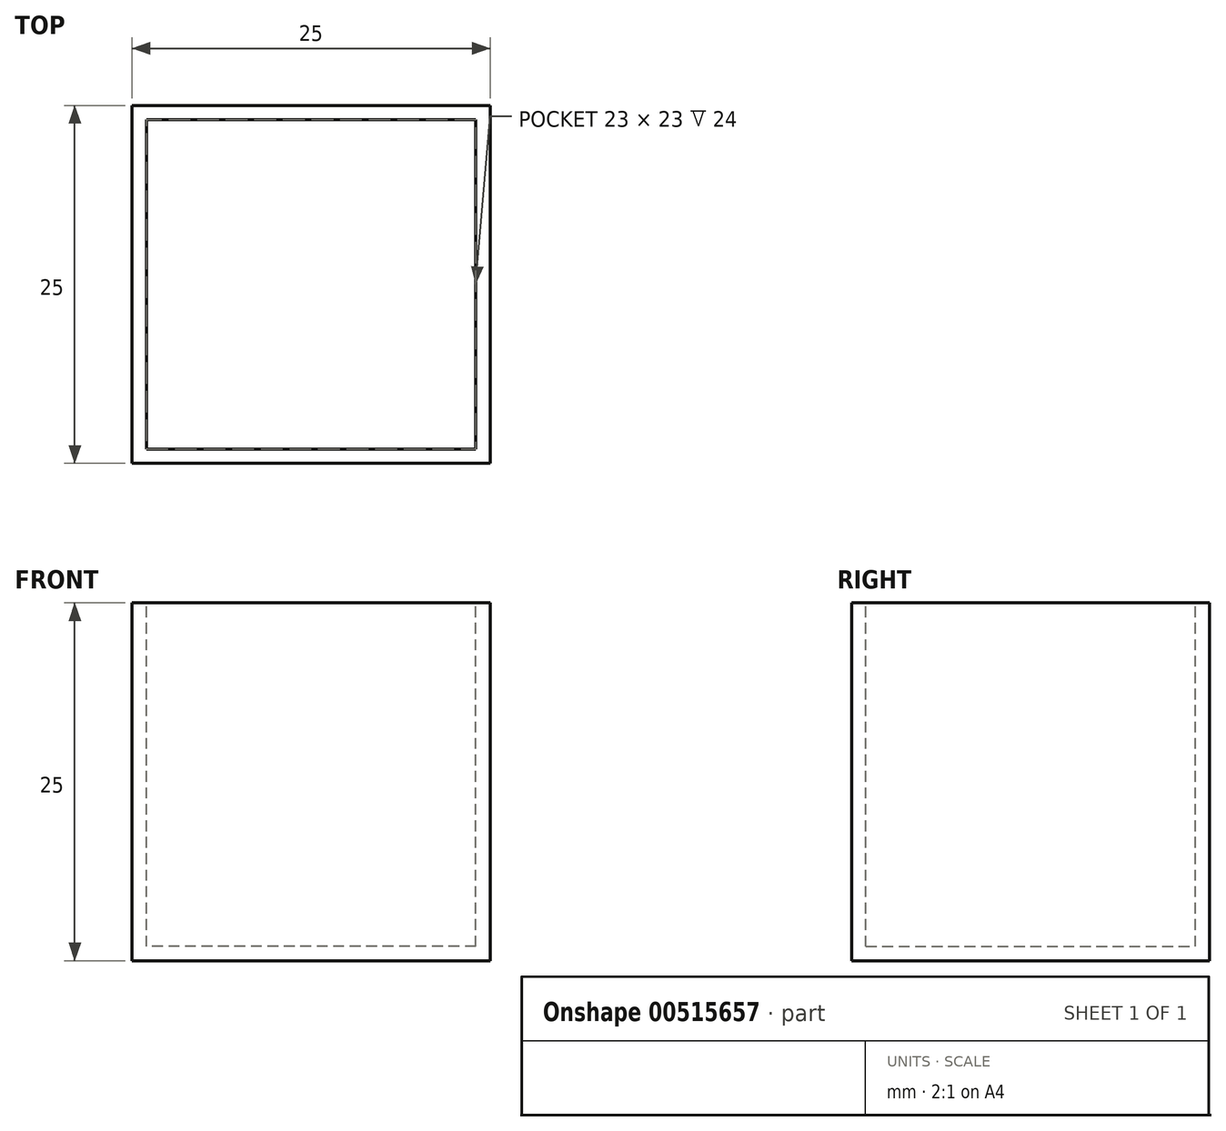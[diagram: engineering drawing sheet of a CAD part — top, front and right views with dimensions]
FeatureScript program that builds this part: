
annotation { "Feature Type Name" : "Feature", "Feature Type Description" : "" }
export const myFeature = defineFeature(function(context is Context, id is Id, definition is map)
    precondition{}
    {
        {
            var Q0;
            Q0=qCreatedBy(makeId("Top.planeOp"),FACE);
            var sketch = newSketch(context, id + "F0", { "sketchPlane" : qUnion([Q0])});
            skLineSegment(sketch, "E0.bottom", {"start": v(12.5, -12.5) * mm, "end": v(-12.5, -12.5) * mm});
            skLineSegment(sketch, "E0.top", {"start": v(12.5, 12.5) * mm, "end": v(-12.5, 12.5) * mm});
            skLineSegment(sketch, "E0.left", {"start": v(12.5, -12.5) * mm, "end": v(12.5, 12.5) * mm});
            skLineSegment(sketch, "E0.right", {"start": v(-12.5, -12.5) * mm, "end": v(-12.5, 12.5) * mm});
            skPoint(sketch, "E0.middle", {"position": v(0, 0) * mm});
            skSolve(sketch);
        }
        {
            var Q0;
            Q0=makeQuery(id+"F0.imprint","IMPRINT",FACE,{"disambiguationData":[TD([[makeQuery(id+"F0.imprint","IMPRINT",EDGE,{"derivedFrom":sQuery(id+"F0.wireOp",EDGE,"E0.bottom")}),-1.0]])]});
            extrude(context, id + "F1", {"entities" : qUnion([Q0]), "depth" : 25 * mm, "offsetDistance" : 25 * mm});
        }
        {
            var Q0;
            Q0=makeQuery(id+"F1.opExtrude","CAP_FACE",FACE,{"disambiguationData":[OSD([sQuery(id+"F0.wireOp",EDGE,"E0.bottom"),sQuery(id+"F0.wireOp",EDGE,"E0.top"),sQuery(id+"F0.wireOp",EDGE,"E0.left"),sQuery(id+"F0.wireOp",EDGE,"E0.right")])],"isStart":false});
            var sketch = newSketch(context, id + "F2", { "sketchPlane" : qUnion([Q0])});
            skLineSegment(sketch, "E1.bottom", {"start": v(11.5, -11.5) * mm, "end": v(-11.5, -11.5) * mm});
            skLineSegment(sketch, "E1.top", {"start": v(11.5, 11.5) * mm, "end": v(-11.5, 11.5) * mm});
            skLineSegment(sketch, "E1.left", {"start": v(11.5, -11.5) * mm, "end": v(11.5, 11.5) * mm});
            skLineSegment(sketch, "E1.right", {"start": v(-11.5, -11.5) * mm, "end": v(-11.5, 11.5) * mm});
            skPoint(sketch, "E1.middle", {"position": v(0, 0) * mm});
            skPoint(sketch, "E2", {"position": v(0, -11.5) * mm});
            skPoint(sketch, "E3", {"position": v(0, -12.5) * mm});
            skPoint(sketch, "E4", {"position": v(12.5, 0) * mm});
            skPoint(sketch, "E5", {"position": v(11.5, 0) * mm});
            skSolve(sketch);
        }
        {
            var Q0;
            Q0=makeQuery(id+"F2.imprint","IMPRINT",FACE,{"disambiguationData":[TD([[makeQuery(id+"F2.imprint","IMPRINT",EDGE,{"derivedFrom":sQuery(id+"F2.wireOp",EDGE,"E1.bottom")}),-1.0]])]});
            extrude(context, id + "F3", {"entities" : qUnion([Q0]), "operationType" : NewBodyOperationType.REMOVE, "oppositeDirection" : true, "depth" : 24 * mm, "offsetDistance" : 25 * mm});
        }
    });
